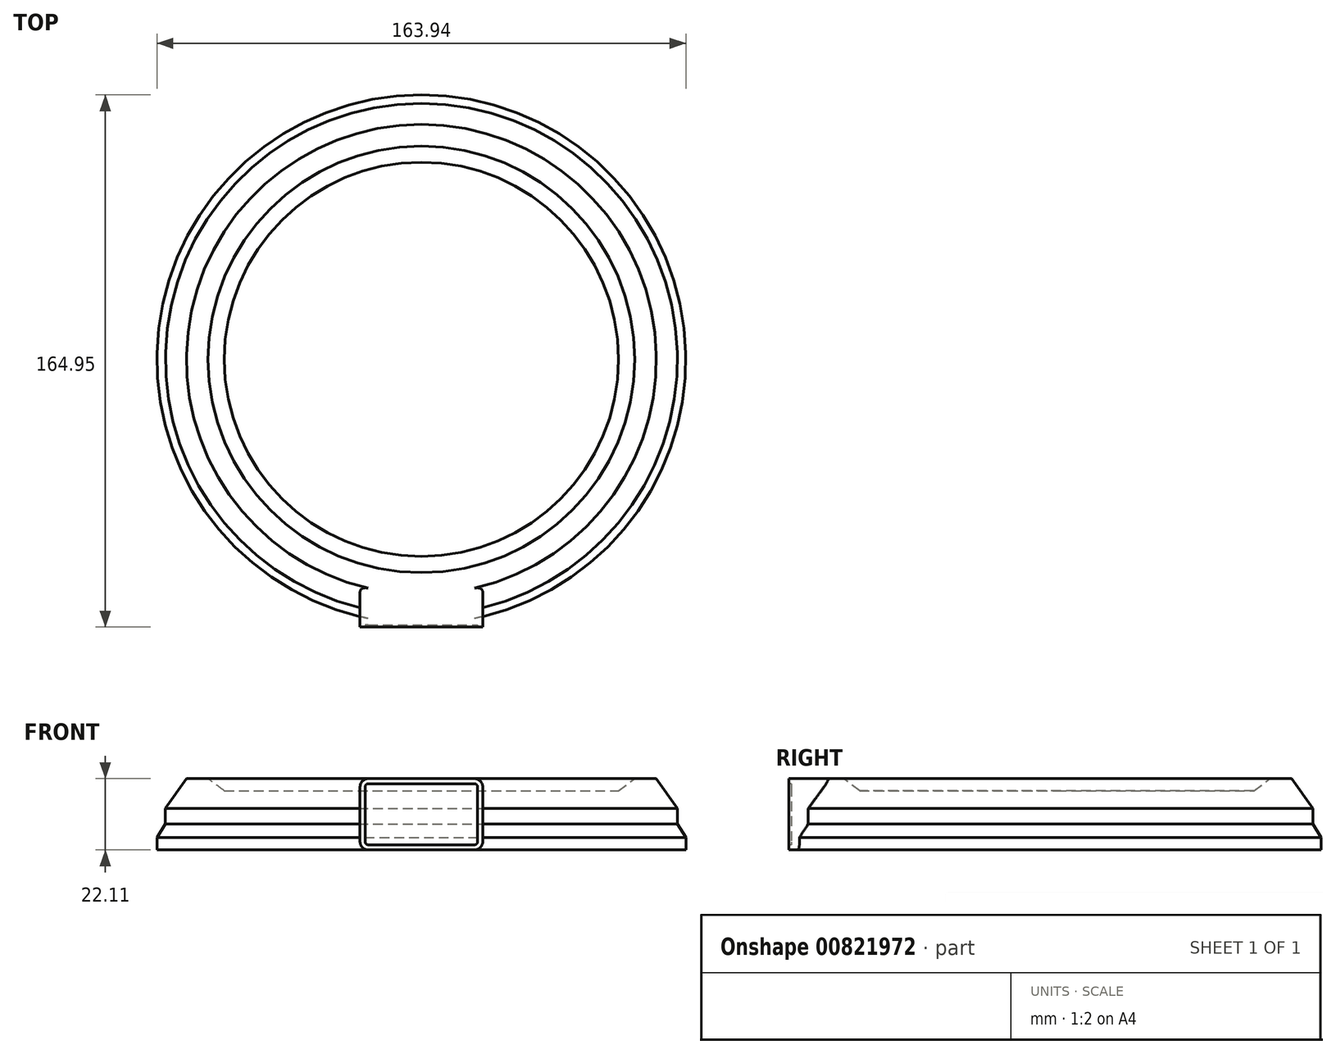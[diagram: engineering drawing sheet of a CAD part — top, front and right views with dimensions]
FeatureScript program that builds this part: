
annotation { "Feature Type Name" : "Feature", "Feature Type Description" : "" }
export const myFeature = defineFeature(function(context is Context, id is Id, definition is map)
    precondition{}
    {
        {
            var Q0;
            Q0=qCreatedBy(makeId("Front.planeOp"),FACE);
            var sketch = newSketch(context, id + "F0", { "sketchPlane" : qUnion([Q0])});
            skLineSegment(sketch, "E0", {"start": v(0, 0) * mm, "end": v(0, 18.38) * mm});
            skLineSegment(sketch, "E1", {"start": v(0, 18.38) * mm, "end": v(61.1, 18.38) * mm});
            skLineSegment(sketch, "E2", {"start": v(61.1, 18.38) * mm, "end": v(66.12, 22.1) * mm});
            skLineSegment(sketch, "E3", {"start": v(66.12, 22.1) * mm, "end": v(72.81, 22.1) * mm});
            skLineSegment(sketch, "E4", {"start": v(79.34, 12.84) * mm, "end": v(79.34, 8.06) * mm});
            skLineSegment(sketch, "E5", {"start": v(79.34, 8.06) * mm, "end": v(81.97, 3.91) * mm});
            skLineSegment(sketch, "E6", {"start": v(81.97, 3.91) * mm, "end": v(81.97, 0) * mm});
            skLineSegment(sketch, "E7", {"start": v(81.97, 0) * mm, "end": v(0, 0) * mm});
            skLineSegment(sketch, "E8", {"start": v(72.81, 22.1) * mm, "end": v(79.34, 12.84) * mm});
            skSolve(sketch);
        }
        {
            var Q0;
            Q0=makeQuery(id+"F0.imprint","IMPRINT",FACE,{"disambiguationData":[TD([[makeQuery(id+"F0.imprint","IMPRINT",EDGE,{"derivedFrom":sQuery(id+"F0.wireOp",EDGE,"E0")}),-1.0]])]});
            var Q1;
            Q1=sQuery(id+"F0.wireOp",EDGE,"E0");
            revolve(context, id + "F1", {"surfaceOperationType" : NewSurfaceOperationType.NEW, "entities" : qUnion([Q0]), "axis" : qUnion([Q1]), "revolveType" : RevolveType.FULL});
        }
        {
            var Q0;
            Q0=qCreatedBy(makeId("Front.planeOp"),FACE);
            cPlane(context, id + "F2", {"entities" : qUnion([Q0]), "cplaneType" : CPlaneType.OFFSET, "offset" : 79.48 * mm, "width" : 150 * mm, "height" : 150 * mm});
        }
        {
            var Q0;
            Q0=qCreatedBy(id+"F2.planeOp",FACE);
            var sketch = newSketch(context, id + "F3", { "sketchPlane" : qUnion([Q0])});
            skLineSegment(sketch, "E9.bottom", {"start": v(-19, 22.1) * mm, "end": v(19, 22.1) * mm});
            skLineSegment(sketch, "E9.top", {"start": v(-19, 2.77) * mm, "end": v(19, 2.77) * mm});
            skLineSegment(sketch, "E9.left", {"start": v(-19, 22.1) * mm, "end": v(-19, 2.77) * mm});
            skLineSegment(sketch, "E9.right", {"start": v(19, 22.1) * mm, "end": v(19, 2.77) * mm});
            skLineSegment(sketch, "E10.0", {"start": v(72.81, 22.1) * mm, "end": v(-72.81, 22.1) * mm, "construction": true});
            skSolve(sketch);
        }
        {
            var Q0;
            Q0=makeQuery(id+"F3.imprint","IMPRINT",FACE,{"disambiguationData":[TD([[makeQuery(id+"F3.imprint","IMPRINT",EDGE,{"derivedFrom":sQuery(id+"F3.wireOp",EDGE,"E9.bottom")}),-1.0]])]});
            extrude(context, id + "F4", {"entities" : qUnion([Q0]), "operationType" : NewBodyOperationType.ADD, "oppositeDirection" : true, "depth" : 12.3 * mm, "offsetDistance" : 25 * mm});
        }
        {
            var Q0;
            Q0=makeQuery(id+"F3.imprint","IMPRINT",FACE,{"disambiguationData":[TD([[makeQuery(id+"F3.imprint","IMPRINT",EDGE,{"derivedFrom":sQuery(id+"F3.wireOp",EDGE,"E9.bottom")}),-1.0]])]});
            extrude(context, id + "F5", {"entities" : qUnion([Q0]), "operationType" : NewBodyOperationType.ADD, "depth" : 3.5 * mm, "offsetDistance" : 25 * mm});
        }
        {
            var Q0;
            Q0=makeQuery(id+"F5.opExtrude","SWEPT_FACE",FACE,{"disambiguationData":[OSD([sQuery(id+"F3.wireOp",EDGE,"E9.top")])]});
            var Q1;
            Q1=makeQuery(id+"F1.opRevolve","SWEPT_FACE",FACE,{"disambiguationData":[OSD([sQuery(id+"F0.wireOp",EDGE,"E7")])]});
            extrude(context, id + "F6", {"entities" : qUnion([Q0]), "operationType" : NewBodyOperationType.ADD, "endBound" : BoundingType.UP_TO_SURFACE, "depth" : 25 * mm, "endBoundEntityFace" : qUnion([Q1]), "offsetDistance" : 25 * mm});
        }
        {
            var Q0;
            {var subQ0=sQuery(id+"F3.wireOp",EDGE,"E9.left");var subQ1=sQuery(id+"F3.wireOp",EDGE,"E9.bottom");Q0=makeQuery(id+"F5.boolean.opBoolean","MERGE",EDGE,{"derivedFrom":[makeQuery(id+"F4.opExtrude","SWEPT_EDGE",EDGE,{"disambiguationData":[OSD([subQ1,subQ0])]}),makeQuery(id+"F5.opExtrude","SWEPT_EDGE",EDGE,{"disambiguationData":[OSD([subQ1,subQ0])]})]});}
            var Q1;
            {var subQ0=sQuery(id+"F3.wireOp",EDGE,"E9.right");var subQ1=sQuery(id+"F3.wireOp",EDGE,"E9.bottom");Q1=makeQuery(id+"F5.boolean.opBoolean","MERGE",EDGE,{"derivedFrom":[makeQuery(id+"F4.opExtrude","SWEPT_EDGE",EDGE,{"disambiguationData":[OSD([subQ1,subQ0])]}),makeQuery(id+"F5.opExtrude","SWEPT_EDGE",EDGE,{"disambiguationData":[OSD([subQ1,subQ0])]})]});}
            var Q2;
            Q2=makeQuery(id+"F6.opExtrude","CAP_EDGE",EDGE,{"disambiguationData":[OSD([sQuery(id+"F3.wireOp",EDGE,"E9.top"),sQuery(id+"F3.wireOp",EDGE,"E9.right")])],"isStart":false});
            var Q3;
            Q3=makeQuery(id+"F6.opExtrude","CAP_EDGE",EDGE,{"disambiguationData":[OSD([sQuery(id+"F3.wireOp",EDGE,"E9.top"),sQuery(id+"F3.wireOp",EDGE,"E9.left")])],"isStart":false});
            fillet(context, id + "F7", {"entities" : qUnion([Q0, Q1, Q2, Q3]), "radius" : 2.5 * mm, "tangentPropagation" : true, "allowEdgeOverflow" : false});
        }
        {
            var Q0;
            {var subQ0=sQuery(id+"F3.wireOp",EDGE,"E9.top");Q0=makeQuery(id+"F6.boolean.opBoolean","MERGE",FACE,{"derivedFrom":[makeQuery(id+"F5.opExtrude","CAP_FACE",FACE,{"disambiguationData":[OSD([sQuery(id+"F3.wireOp",EDGE,"E9.bottom"),subQ0,sQuery(id+"F3.wireOp",EDGE,"E9.left"),sQuery(id+"F3.wireOp",EDGE,"E9.right")])],"isStart":false}),makeQuery(id+"F6.opExtrude","SWEPT_FACE",FACE,{"disambiguationData":[OSD([subQ0])]})]});}
            var sketch = newSketch(context, id + "F8", { "sketchPlane" : qUnion([Q0])});
            skArc(sketch, "E11.0", {"start": v(-16.5, 20.5) * mm, "mid": v(-17.14, 20.24) * mm, "end": v(-17.4, 19.6) * mm});
            skLineSegment(sketch, "E11.1", {"start": v(-17.4, 19.6) * mm, "end": v(-17.4, 2.5) * mm});
            skLineSegment(sketch, "E11.2", {"start": v(-16.5, 20.5) * mm, "end": v(16.5, 20.5) * mm});
            skArc(sketch, "E11.3", {"start": v(-17.4, 2.5) * mm, "mid": v(-17.14, 1.86) * mm, "end": v(-16.5, 1.6) * mm});
            skArc(sketch, "E11.4", {"start": v(17.4, 19.6) * mm, "mid": v(17.14, 20.24) * mm, "end": v(16.5, 20.5) * mm});
            skLineSegment(sketch, "E11.5", {"start": v(17.4, 19.6) * mm, "end": v(17.4, 2.5) * mm});
            skArc(sketch, "E11.6", {"start": v(16.5, 1.6) * mm, "mid": v(17.14, 1.86) * mm, "end": v(17.4, 2.5) * mm});
            skLineSegment(sketch, "E11.7", {"start": v(16.5, 1.6) * mm, "end": v(-16.5, 1.6) * mm});
            skSolve(sketch);
        }
        {
            var Q0;
            Q0=makeQuery(id+"F8.imprint","IMPRINT",FACE,{"disambiguationData":[TD([[makeQuery(id+"F8.imprint","IMPRINT",EDGE,{"derivedFrom":sQuery(id+"F8.wireOp",EDGE,"E11.0")}),1.0]])]});
            extrude(context, id + "F9", {"entities" : qUnion([Q0]), "operationType" : NewBodyOperationType.REMOVE, "oppositeDirection" : true, "depth" : 0.7 * mm, "offsetDistance" : 25 * mm});
        }
    });
